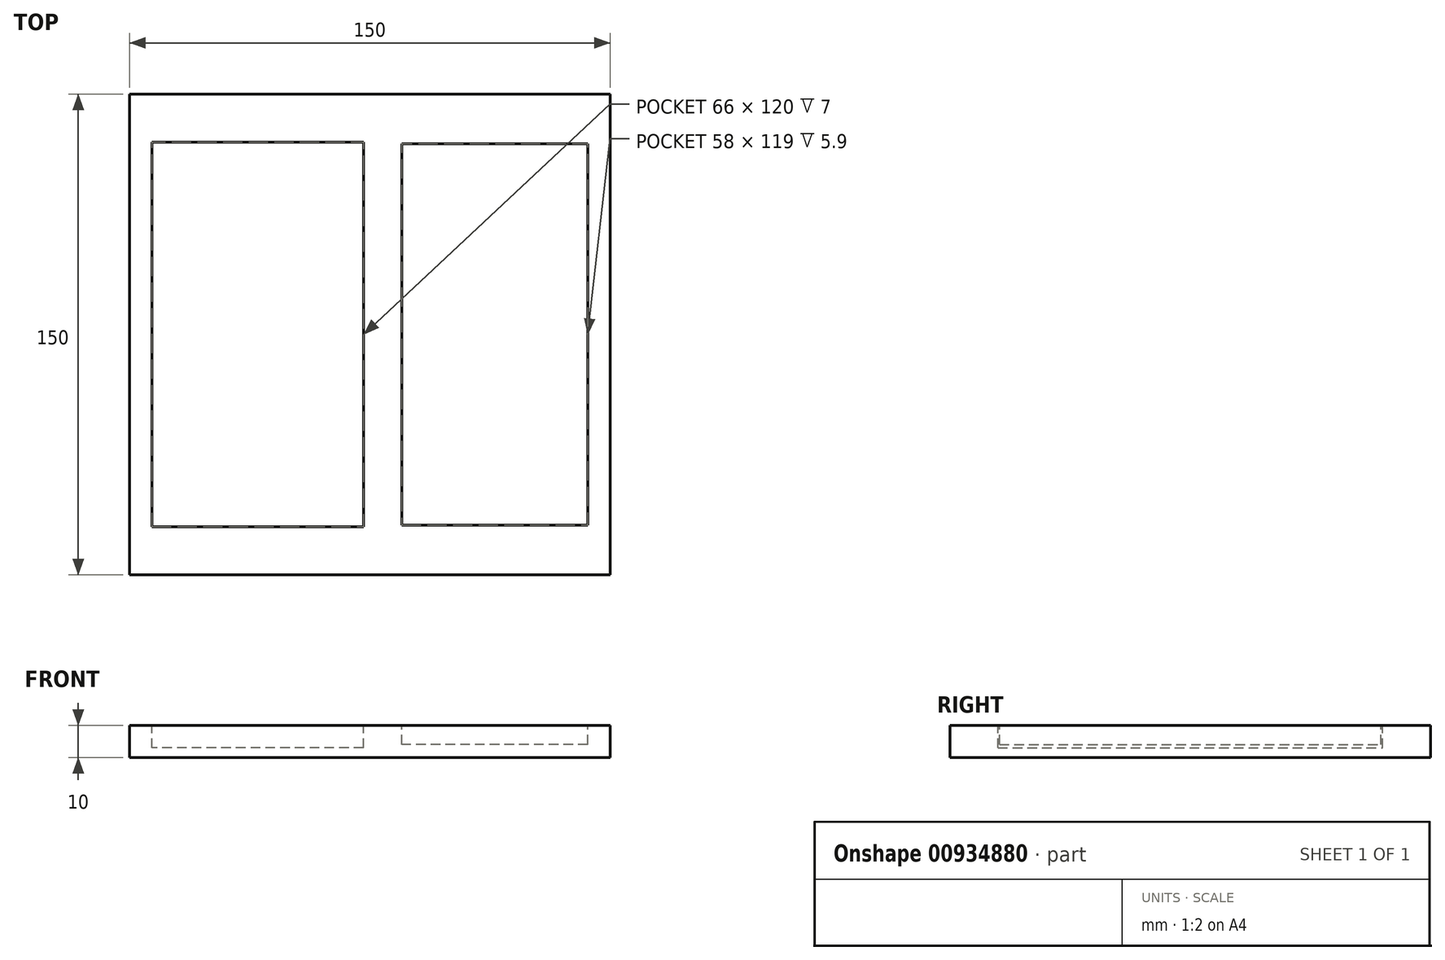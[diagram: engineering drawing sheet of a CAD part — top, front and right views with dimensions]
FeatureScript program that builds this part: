
annotation { "Feature Type Name" : "Feature", "Feature Type Description" : "" }
export const myFeature = defineFeature(function(context is Context, id is Id, definition is map)
    precondition{}
    {
        {
            var Q0;
            Q0=qCreatedBy(makeId("Top.planeOp"),FACE);
            var sketch = newSketch(context, id + "F0", { "sketchPlane" : qUnion([Q0])});
            skLineSegment(sketch, "E0.bottom", {"start": v(75, -75) * mm, "end": v(-75, -75) * mm});
            skLineSegment(sketch, "E0.top", {"start": v(75, 75) * mm, "end": v(-75, 75) * mm});
            skLineSegment(sketch, "E0.left", {"start": v(75, -75) * mm, "end": v(75, 75) * mm});
            skLineSegment(sketch, "E0.right", {"start": v(-75, -75) * mm, "end": v(-75, 75) * mm});
            skPoint(sketch, "E0.middle", {"position": v(0, 0) * mm});
            skSolve(sketch);
        }
        {
            var Q0;
            Q0=makeQuery(id+"F0.imprint","IMPRINT",FACE,{"disambiguationData":[TD([[makeQuery(id+"F0.imprint","IMPRINT",EDGE,{"derivedFrom":sQuery(id+"F0.wireOp",EDGE,"E0.bottom")}),-1.0]])]});
            extrude(context, id + "F1", {"entities" : qUnion([Q0]), "depth" : 10 * mm, "offsetDistance" : 25 * mm});
        }
        {
            var Q0;
            Q0=makeQuery(id+"F1.opExtrude","CAP_FACE",FACE,{"disambiguationData":[OSD([sQuery(id+"F0.wireOp",EDGE,"E0.bottom"),sQuery(id+"F0.wireOp",EDGE,"E0.top"),sQuery(id+"F0.wireOp",EDGE,"E0.left"),sQuery(id+"F0.wireOp",EDGE,"E0.right")])],"isStart":false});
            var sketch = newSketch(context, id + "F2", { "sketchPlane" : qUnion([Q0])});
            skLineSegment(sketch, "E1.bottom", {"start": v(-2, -60) * mm, "end": v(-68, -60) * mm});
            skLineSegment(sketch, "E1.top", {"start": v(-2, 60) * mm, "end": v(-68, 60) * mm});
            skLineSegment(sketch, "E1.left", {"start": v(-2, -60) * mm, "end": v(-2, 60) * mm});
            skLineSegment(sketch, "E1.right", {"start": v(-68, -60) * mm, "end": v(-68, 60) * mm});
            skPoint(sketch, "E1.middle", {"position": v(-35, 0) * mm});
            skSolve(sketch);
        }
        {
            var Q0;
            Q0=makeQuery(id+"F2.imprint","IMPRINT",FACE,{"disambiguationData":[TD([[makeQuery(id+"F2.imprint","IMPRINT",EDGE,{"derivedFrom":sQuery(id+"F2.wireOp",EDGE,"E1.bottom")}),-1.0]])]});
            var Q1;
            Q1=makeQuery(id+"F2.imprint","IMPRINT",FACE,{"disambiguationData":[TD([[makeQuery(id+"F2.imprint","IMPRINT",EDGE,{"derivedFrom":sQuery(id+"F2.wireOp",EDGE,"IzZhZOKF-Ewwd-JL7X-PO1s-cMWClLe1jrfB.bottom")}),-1.0]])]});
            extrude(context, id + "F3", {"entities" : qUnion([Q0, Q1]), "operationType" : NewBodyOperationType.REMOVE, "oppositeDirection" : true, "depth" : 7 * mm, "offsetDistance" : 25 * mm});
        }
        {
            var Q0;
            Q0=makeQuery(id+"F1.opExtrude","CAP_FACE",FACE,{"disambiguationData":[OSD([sQuery(id+"F0.wireOp",EDGE,"E0.bottom"),sQuery(id+"F0.wireOp",EDGE,"E0.top"),sQuery(id+"F0.wireOp",EDGE,"E0.left"),sQuery(id+"F0.wireOp",EDGE,"E0.right")])],"isStart":false});
            var sketch = newSketch(context, id + "F4", { "sketchPlane" : qUnion([Q0])});
            skLineSegment(sketch, "E2.bottom", {"start": v(68, -59.5) * mm, "end": v(10, -59.5) * mm});
            skLineSegment(sketch, "E2.top", {"start": v(68, 59.5) * mm, "end": v(10, 59.5) * mm});
            skLineSegment(sketch, "E2.left", {"start": v(68, -59.5) * mm, "end": v(68, 59.5) * mm});
            skLineSegment(sketch, "E2.right", {"start": v(10, -59.5) * mm, "end": v(10, 59.5) * mm});
            skPoint(sketch, "E2.middle", {"position": v(39, 0) * mm});
            skSolve(sketch);
        }
        {
            var Q0;
            Q0 = qSketchRegion(id + "F4", true);
            extrude(context, id + "F5", {"entities" : qUnion([Q0]), "operationType" : NewBodyOperationType.REMOVE, "oppositeDirection" : true, "depth" : 5.9 * mm, "offsetDistance" : 25 * mm});
        }
    });
